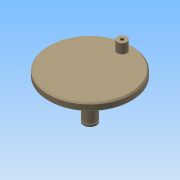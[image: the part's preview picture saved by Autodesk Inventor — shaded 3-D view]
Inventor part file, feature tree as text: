
AUTODESK INVENTOR PART (.ipt)
format: ipt  version: 2015 (Build 190159000, 159)  size: 129,536 bytes
history: native  units: mm
features: sketch x6, extrude x5, chamfer x2, thread x1, revolve x1
ambient origin geometry x8: Origin, YZ Plane, XZ Plane, XY Plane, X Axis, Y Axis, Z Axis, Center Point
bodies: 实体1 (feature_tree)
feature tree (15):
  extrude  "拉伸1"  Depth=12.0mm TaperAngle=0.0deg
  extrude  "拉伸2"  Depth=15.0mm
  extrude  "拉伸3"  Depth=15.0mm TaperAngle=0.0deg
  thread  "螺纹1"  [1 undecoded]
  extrude  "拉伸4"  Depth=10.0mm TaperAngle=0.0deg
  extrude  "拉伸5"  Depth=59.7mm TaperAngle=0.0deg
  chamfer  "倒角1"  Distance=3.0mm
  chamfer  "倒角2"  Distance=2.0mm Angle=45.0deg
  revolve  "旋转1"  Angle=45.0deg
  sketch  "草图1"  dims[d0=130.0mm d1=12.0mm d2=0.0mm]
  sketch  "草图2"  dims[d3=100.0mm d4=15.0mm]
  sketch  "草图3"  dims[d5=11.389689mm d6=15.0mm d7=0.0mm d8=5.0mm]
  sketch  "草图4"  dims[d9=12.0mm d10=0.0mm d11=10.0mm d12=0.0mm]
  sketch  "草图5"  dims[d13=20.0mm d14=59.7mm d15=0.0mm]
  sketch  "草图6"  dims[d16=26.0mm d17=3.0mm d18=0.0mm d19=2.0mm d20=2.0mm d21=45.0deg d22=0.5mm d23=2.0mm d24=45.0deg d25=10.293164mm d26=4.0mm d27=1.2mm d28=9.175mm d29=9.275965mm d30=90.0deg]
note: 1 required parameter value undecoded (feature->parameter linkage not recoverable at this tier; creation-order binding heuristic only, values carry confidence <= 0.55)
